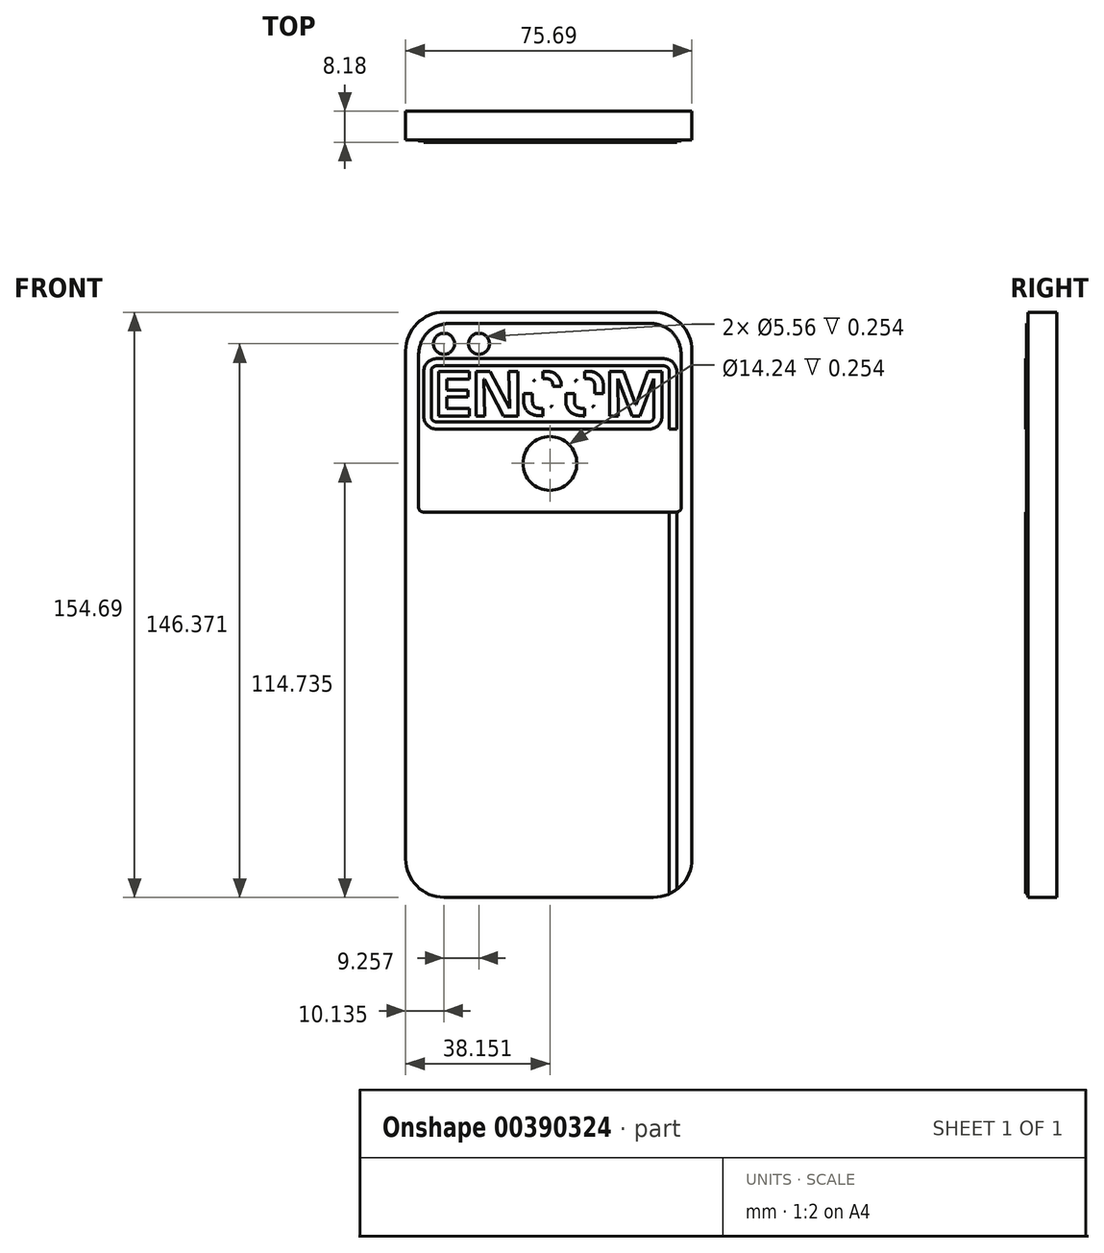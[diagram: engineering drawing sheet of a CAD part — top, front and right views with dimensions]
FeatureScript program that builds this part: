
annotation { "Feature Type Name" : "Feature", "Feature Type Description" : "" }
export const myFeature = defineFeature(function(context is Context, id is Id, definition is map)
    precondition{}
    {
        {
            var Q0;
            Q0=qCreatedBy(makeId("Front.planeOp"),FACE);
            var sketch = newSketch(context, id + "F0", { "sketchPlane" : qUnion([Q0])});
            skLineSegment(sketch, "E0.bottom", {"start": v(201.26, 129.6) * mm, "end": v(256.63, 129.6) * mm});
            skLineSegment(sketch, "E0.top", {"start": v(201.26, -25.09) * mm, "end": v(256.63, -25.09) * mm});
            skLineSegment(sketch, "E0.left", {"start": v(191.1, 119.44) * mm, "end": v(191.1, -14.93) * mm});
            skLineSegment(sketch, "E0.right", {"start": v(266.8, 119.44) * mm, "end": v(266.8, -14.93) * mm});
            skPoint(sketch, "E1.visualSharp", {"position": v(191.1, 129.6) * mm});
            skArc(sketch, "E1.filletArc", {"start": v(201.26, 129.6) * mm, "mid": v(194.08, 126.62) * mm, "end": v(191.1, 119.44) * mm});
            skPoint(sketch, "E2.visualSharp", {"position": v(266.8, 129.6) * mm});
            skArc(sketch, "E2.filletArc", {"start": v(266.8, 119.44) * mm, "mid": v(263.82, 126.62) * mm, "end": v(256.63, 129.6) * mm});
            skPoint(sketch, "E3.visualSharp", {"position": v(266.8, -25.09) * mm});
            skArc(sketch, "E3.filletArc", {"start": v(256.63, -25.09) * mm, "mid": v(263.82, -22.1) * mm, "end": v(266.8, -14.93) * mm});
            skPoint(sketch, "E4.visualSharp", {"position": v(191.1, -25.09) * mm});
            skArc(sketch, "E4.filletArc", {"start": v(191.1, -14.93) * mm, "mid": v(194.08, -22.1) * mm, "end": v(201.26, -25.09) * mm});
            skCircle(sketch, "E5", {"center": v(201.23, 121.28) * mm, "radius": 2.78 * mm});
            skCircle(sketch, "E6", {"center": v(210.5, 121.28) * mm, "radius": 2.78 * mm});
            skCircle(sketch, "E7", {"center": v(229.25, 89.64) * mm, "radius": 7.12 * mm});
            skLineSegment(sketch, "E8", {"start": v(229.25, 129.6) * mm, "end": v(229.25, -25.09) * mm});
            skLineSegment(sketch, "E9", {"start": v(229.25, 76.81) * mm, "end": v(195.67, 76.81) * mm});
            skLineSegment(sketch, "E10", {"start": v(194.55, 77.93) * mm, "end": v(194.55, 118.32) * mm});
            skPoint(sketch, "E11.visualSharp", {"position": v(194.55, 76.81) * mm});
            skArc(sketch, "E11.filletArc", {"start": v(194.55, 77.93) * mm, "mid": v(194.88, 77.14) * mm, "end": v(195.67, 76.81) * mm});
            skArc(sketch, "E12.MirrorCS", {"start": v(263.96, 77.93) * mm, "mid": v(263.63, 77.14) * mm, "end": v(262.83, 76.81) * mm});
            skLineSegment(sketch, "E13.MirrorCS", {"start": v(229.25, 76.81) * mm, "end": v(262.83, 76.81) * mm});
            skLineSegment(sketch, "E14.MirrorCS", {"start": v(263.96, 77.93) * mm, "end": v(263.96, 118.32) * mm});
            skLineSegment(sketch, "E15", {"start": v(195.67, 77.93) * mm, "end": v(229.25, 77.93) * mm});
            skLineSegment(sketch, "E16", {"start": v(195.67, 77.93) * mm, "end": v(195.67, 118.32) * mm});
            skLineSegment(sketch, "E17.MirrorCS", {"start": v(262.83, 77.93) * mm, "end": v(229.25, 77.93) * mm});
            skLineSegment(sketch, "E18.MirrorCS", {"start": v(262.83, 77.93) * mm, "end": v(262.83, 118.32) * mm});
            skLineSegment(sketch, "E19", {"start": v(229.25, 97.2) * mm, "end": v(195.67, 97.2) * mm});
            skLineSegment(sketch, "E20", {"start": v(195.67, 118.32) * mm, "end": v(229.25, 118.32) * mm});
            skArc(sketch, "E21", {"start": v(194.55, 118.32) * mm, "mid": v(194.96, 120.97) * mm, "end": v(196.15, 123.36) * mm});
            skArc(sketch, "E22", {"start": v(196.15, 123.36) * mm, "mid": v(197.4, 124.73) * mm, "end": v(198.94, 125.74) * mm});
            skArc(sketch, "E23", {"start": v(198.94, 125.74) * mm, "mid": v(200.66, 126.38) * mm, "end": v(202.48, 126.67) * mm});
            skLineSegment(sketch, "E24", {"start": v(202.48, 126.67) * mm, "end": v(229.25, 126.67) * mm});
            skLineSegment(sketch, "E25.MirrorCS", {"start": v(262.83, 118.32) * mm, "end": v(229.25, 118.32) * mm});
            skArc(sketch, "E26.MirrorCS", {"start": v(263.96, 118.32) * mm, "mid": v(263.55, 120.97) * mm, "end": v(262.36, 123.36) * mm});
            skArc(sketch, "E27.MirrorCS", {"start": v(262.36, 123.36) * mm, "mid": v(261.1, 124.73) * mm, "end": v(259.57, 125.74) * mm});
            skArc(sketch, "E28.MirrorCS", {"start": v(259.57, 125.74) * mm, "mid": v(257.84, 126.38) * mm, "end": v(256.02, 126.67) * mm});
            skLineSegment(sketch, "E29.MirrorCS", {"start": v(256.02, 126.67) * mm, "end": v(229.25, 126.67) * mm});
            skLineSegment(sketch, "E30.MirrorCS", {"start": v(229.25, 97.2) * mm, "end": v(262.83, 97.2) * mm});
            skSolve(sketch);
        }
        {
            var Q0;
            Q0=qSketchRegion(id+"F0",true);
            var Q1;
            Q1=makeQuery(id+"F0.imprint","IMPRINT",FACE,{"disambiguationData":[TD([[makeQuery(id+"F0.imprint","IMPRINT",EDGE,{"derivedFrom":sQuery(id+"F0.wireOp",EDGE,"E6")}),1.0]])]});
            var Q2;
            Q2=makeQuery(id+"F0.imprint","IMPRINT",FACE,{"disambiguationData":[TD([[makeQuery(id+"F0.imprint","IMPRINT",EDGE,{"derivedFrom":sQuery(id+"F0.wireOp",EDGE,"E5")}),1.0]])]});
            var Q3;
            {var subQ0=sQuery(id+"F0.wireOp",EDGE,"E19");Q3=makeQuery(id+"F0.imprint","IMPRINT",FACE,{"disambiguationData":[TD([[makeQuery(id+"F0.imprint","IMPRINT",EDGE,{"derivedFrom":subQ0}),-1.0]])]});}
            var Q4;
            {var subQ2=sQuery(id+"F0.wireOp",EDGE,"E25.MirrorCS");Q4=makeQuery(id+"F0.imprint","IMPRINT",FACE,{"disambiguationData":[TD([[makeQuery(id+"F0.imprint","IMPRINT",EDGE,{"derivedFrom":subQ2}),1.0]])]});}
            var Q5;
            {var subQ0=sQuery(id+"F0.wireOp",EDGE,"E17.MirrorCS");Q5=makeQuery(id+"F0.imprint","IMPRINT",FACE,{"disambiguationData":[TD([[makeQuery(id+"F0.imprint","IMPRINT",EDGE,{"derivedFrom":subQ0}),-1.0]])]});}
            var Q6;
            {var subQ0=sQuery(id+"F0.wireOp",EDGE,"E8");var subQ1=sQuery(id+"F0.wireOp",EDGE,"E7");var subQ2=makeQuery(id+"F0.imprint","INTERSECT",VERTEX,{"disambiguationData":[OD(0.0)],"derivedFrom":[subQ1,subQ0]});Q6=makeQuery(id+"F0.imprint","IMPRINT",FACE,{"disambiguationData":[TD([[makeQuery(id+"F0.imprint","IMPRINT",EDGE,{"disambiguationData":[TD([[subQ2,1.0]])],"derivedFrom":subQ1}),1.0]])]});}
            var Q7;
            {var subQ0=sQuery(id+"F0.wireOp",EDGE,"E8");var subQ1=sQuery(id+"F0.wireOp",EDGE,"E7");var subQ2=makeQuery(id+"F0.imprint","INTERSECT",VERTEX,{"disambiguationData":[OD(0.0)],"derivedFrom":[subQ1,subQ0]});Q7=makeQuery(id+"F0.imprint","IMPRINT",FACE,{"disambiguationData":[TD([[makeQuery(id+"F0.imprint","IMPRINT",EDGE,{"disambiguationData":[TD([[subQ2,-1.0]])],"derivedFrom":subQ1}),1.0]])]});}
            var Q8;
            {var subQ4=sQuery(id+"F0.wireOp",EDGE,"E13.MirrorCS");Q8=makeQuery(id+"F0.imprint","IMPRINT",FACE,{"disambiguationData":[TD([[makeQuery(id+"F0.imprint","IMPRINT",EDGE,{"derivedFrom":subQ4}),1.0]])]});}
            var Q9;
            Q9=makeQuery(id+"F0.imprint","IMPRINT",FACE,{"disambiguationData":[TD([[makeQuery(id+"F0.imprint","IMPRINT",EDGE,{"derivedFrom":sQuery(id+"F0.wireOp",EDGE,"E5")}),-1.0]])]});
            var Q10;
            {var subQ0=sQuery(id+"F0.wireOp",EDGE,"E15");Q10=makeQuery(id+"F0.imprint","IMPRINT",FACE,{"disambiguationData":[TD([[makeQuery(id+"F0.imprint","IMPRINT",EDGE,{"derivedFrom":subQ0}),1.0]])]});}
            extrude(context, id + "F1", {"entities" : qUnion([Q0, Q1, Q2, Q3, Q4, Q5, Q6, Q7, Q8, Q9, Q10]), "oppositeDirection" : true, "depth" : 7.62 * mm});
        }
        {
            var Q0;
            {var subQ4=sQuery(id+"F0.wireOp",EDGE,"E13.MirrorCS");Q0=makeQuery(id+"F0.imprint","IMPRINT",FACE,{"disambiguationData":[TD([[makeQuery(id+"F0.imprint","IMPRINT",EDGE,{"derivedFrom":subQ4}),1.0]])]});}
            var Q1;
            Q1=makeQuery(id+"F0.imprint","IMPRINT",FACE,{"disambiguationData":[TD([[makeQuery(id+"F0.imprint","IMPRINT",EDGE,{"derivedFrom":sQuery(id+"F0.wireOp",EDGE,"E5")}),-1.0]])]});
            var Q2;
            {var subQ0=sQuery(id+"F0.wireOp",EDGE,"E19");Q2=makeQuery(id+"F0.imprint","IMPRINT",FACE,{"disambiguationData":[TD([[makeQuery(id+"F0.imprint","IMPRINT",EDGE,{"derivedFrom":subQ0}),-1.0]])]});}
            var Q3;
            {var subQ0=sQuery(id+"F0.wireOp",EDGE,"E15");Q3=makeQuery(id+"F0.imprint","IMPRINT",FACE,{"disambiguationData":[TD([[makeQuery(id+"F0.imprint","IMPRINT",EDGE,{"derivedFrom":subQ0}),1.0]])]});}
            var Q4;
            {var subQ0=sQuery(id+"F0.wireOp",EDGE,"E17.MirrorCS");Q4=makeQuery(id+"F0.imprint","IMPRINT",FACE,{"disambiguationData":[TD([[makeQuery(id+"F0.imprint","IMPRINT",EDGE,{"derivedFrom":subQ0}),-1.0]])]});}
            var Q5;
            {var subQ2=sQuery(id+"F0.wireOp",EDGE,"E25.MirrorCS");Q5=makeQuery(id+"F0.imprint","IMPRINT",FACE,{"disambiguationData":[TD([[makeQuery(id+"F0.imprint","IMPRINT",EDGE,{"derivedFrom":subQ2}),1.0]])]});}
            var Q6;
            Q6=makeQuery(id+"F1.opExtrude","CAP_FACE",FACE,{"disambiguationData":[OSD([sQuery(id+"F0.wireOp",EDGE,"E0.bottom"),sQuery(id+"F0.wireOp",EDGE,"E0.top"),sQuery(id+"F0.wireOp",EDGE,"E0.left"),sQuery(id+"F0.wireOp",EDGE,"E0.right"),sQuery(id+"F0.wireOp",EDGE,"E1.filletArc"),sQuery(id+"F0.wireOp",EDGE,"E2.filletArc"),sQuery(id+"F0.wireOp",EDGE,"E3.filletArc"),sQuery(id+"F0.wireOp",EDGE,"E4.filletArc"),sQuery(id+"F0.wireOp",EDGE,"E9"),sQuery(id+"F0.wireOp",EDGE,"E10"),sQuery(id+"F0.wireOp",EDGE,"E11.filletArc"),sQuery(id+"F0.wireOp",EDGE,"E13.MirrorCS"),sQuery(id+"F0.wireOp",EDGE,"E12.MirrorCS"),sQuery(id+"F0.wireOp",EDGE,"E14.MirrorCS"),sQuery(id+"F0.wireOp",EDGE,"E21"),sQuery(id+"F0.wireOp",EDGE,"E22"),sQuery(id+"F0.wireOp",EDGE,"E23"),sQuery(id+"F0.wireOp",EDGE,"E24"),sQuery(id+"F0.wireOp",EDGE,"E26.MirrorCS"),sQuery(id+"F0.wireOp",EDGE,"E27.MirrorCS"),sQuery(id+"F0.wireOp",EDGE,"E28.MirrorCS"),sQuery(id+"F0.wireOp",EDGE,"E29.MirrorCS")])],"isStart":false});
            extrude(context, id + "F2", {"entities" : qUnion([Q0, Q1, Q2, Q3, Q4, Q5]), "endBoundEntityFace" : qUnion([Q6]), "depth" : 0.25 * mm});
        }
        {
            var Q0;
            Q0=qCreatedBy(makeId("Front.planeOp"),FACE);
            var sketch = newSketch(context, id + "F3", { "sketchPlane" : qUnion([Q0])});
            skLineSegment(sketch, "E31.bottom", {"start": v(195.87, 117.33) * mm, "end": v(197.87, 117.33) * mm});
            skLineSegment(sketch, "E31.top", {"start": v(195.87, 98.73) * mm, "end": v(197.87, 98.73) * mm});
            skLineSegment(sketch, "E31.left", {"start": v(195.87, 117.33) * mm, "end": v(195.87, 98.73) * mm});
            skLineSegment(sketch, "E32.bottom", {"start": v(195.87, 117.33) * mm, "end": v(262.8, 117.33) * mm});
            skLineSegment(sketch, "E32.left", {"start": v(195.87, 117.33) * mm, "end": v(195.87, 115.44) * mm});
            skLineSegment(sketch, "E32.right", {"start": v(262.8, 117.33) * mm, "end": v(262.8, 115.44) * mm});
            skLineSegment(sketch, "E33.bottom", {"start": v(195.87, 98.73) * mm, "end": v(262.8, 98.73) * mm});
            skLineSegment(sketch, "E33.left", {"start": v(195.87, 98.73) * mm, "end": v(195.87, 100.65) * mm});
            skLineSegment(sketch, "E33.right", {"start": v(262.8, 98.73) * mm, "end": v(262.8, 100.65) * mm});
            skLineSegment(sketch, "E34.bottom", {"start": v(262.8, 117.33) * mm, "end": v(260.8, 117.33) * mm});
            skLineSegment(sketch, "E34.top", {"start": v(262.8, 98.73) * mm, "end": v(260.8, 98.73) * mm});
            skLineSegment(sketch, "E34.left", {"start": v(262.8, 117.33) * mm, "end": v(262.8, 98.73) * mm});
            skLineSegment(sketch, "E35", {"start": v(260.8, 115.44) * mm, "end": v(261, 115.69) * mm});
            skLineSegment(sketch, "E36", {"start": v(197.87, 115.44) * mm, "end": v(197.6, 115.77) * mm});
            skLineSegment(sketch, "E37", {"start": v(197.87, 100.64) * mm, "end": v(197.7, 100.52) * mm});
            skLineSegment(sketch, "E38", {"start": v(195.87, 98.73) * mm, "end": v(195.56, 98.32) * mm});
            skLineSegment(sketch, "E39", {"start": v(195.87, 117.33) * mm, "end": v(195.2, 118.18) * mm});
            skLineSegment(sketch, "E40", {"start": v(262.8, 117.33) * mm, "end": v(263.3, 118) * mm});
            skLineSegment(sketch, "E41", {"start": v(262.8, 98.73) * mm, "end": v(263.5, 98.16) * mm});
            skLineSegment(sketch, "E42", {"start": v(258.9, 100.64) * mm, "end": v(259.43, 100.04) * mm});
            skLineSegment(sketch, "E43", {"start": v(260.8, 100.64) * mm, "end": v(261.23, 100.16) * mm});
            skLineSegment(sketch, "E44", {"start": v(197.87, 102.02) * mm, "end": v(197.87, 114.06) * mm});
            skLineSegment(sketch, "E45", {"start": v(199.25, 115.44) * mm, "end": v(259.41, 115.44) * mm});
            skLineSegment(sketch, "E46", {"start": v(260.8, 114.06) * mm, "end": v(260.8, 100.64) * mm});
            skPoint(sketch, "E47.visualSharp", {"position": v(260.8, 115.44) * mm});
            skArc(sketch, "E47.filletArc", {"start": v(260.8, 114.06) * mm, "mid": v(260.4, 115.04) * mm, "end": v(259.41, 115.44) * mm});
            skPoint(sketch, "E48.visualSharp", {"position": v(197.87, 115.44) * mm});
            skArc(sketch, "E48.filletArc", {"start": v(199.25, 115.44) * mm, "mid": v(198.27, 115.04) * mm, "end": v(197.87, 114.06) * mm});
            skLineSegment(sketch, "E49", {"start": v(256.76, 100.64) * mm, "end": v(257.05, 100.32) * mm});
            skLineSegment(sketch, "E50", {"start": v(255.38, 100.64) * mm, "end": v(199.25, 100.64) * mm});
            skPoint(sketch, "E51.visualSharp", {"position": v(197.87, 100.64) * mm});
            skArc(sketch, "E51.filletArc", {"start": v(197.87, 102.02) * mm, "mid": v(198.27, 101.04) * mm, "end": v(199.25, 100.64) * mm});
            skLineSegment(sketch, "E52", {"start": v(256.76, 102.02) * mm, "end": v(256.76, 112.1) * mm});
            skPoint(sketch, "E53.visualSharp", {"position": v(256.76, 100.64) * mm});
            skArc(sketch, "E53.filletArc", {"start": v(255.38, 100.64) * mm, "mid": v(256.36, 101.04) * mm, "end": v(256.76, 102.02) * mm});
            skLineSegment(sketch, "E54", {"start": v(262.8, 98.73) * mm, "end": v(262.8, 117.33) * mm});
            skLineSegment(sketch, "E55", {"start": v(262.8, 117.33) * mm, "end": v(195.87, 117.33) * mm});
            skLineSegment(sketch, "E56", {"start": v(199.76, 102.2) * mm, "end": v(256.76, 102.2) * mm});
            skLineSegment(sketch, "E57", {"start": v(199.76, 102.2) * mm, "end": v(199.76, 113.9) * mm});
            skLineSegment(sketch, "E58", {"start": v(199.76, 113.9) * mm, "end": v(220.72, 113.9) * mm});
            skLineSegment(sketch, "E59", {"start": v(220.72, 113.9) * mm, "end": v(220.72, 102.2) * mm});
            skLineSegment(sketch, "E60", {"start": v(211.79, 112) * mm, "end": v(212.02, 102.2) * mm});
            skLineSegment(sketch, "E61", {"start": v(211.79, 112) * mm, "end": v(211.87, 112) * mm});
            skLineSegment(sketch, "E62", {"start": v(211.87, 112) * mm, "end": v(216.92, 102.2) * mm});
            skLineSegment(sketch, "E63", {"start": v(218.62, 104.13) * mm, "end": v(218.43, 113.9) * mm});
            skLineSegment(sketch, "E64", {"start": v(218.62, 104.13) * mm, "end": v(218.56, 104.13) * mm});
            skLineSegment(sketch, "E65", {"start": v(218.56, 104.13) * mm, "end": v(213.46, 113.9) * mm});
            skLineSegment(sketch, "E66", {"start": v(209.7, 102.2) * mm, "end": v(209.7, 113.9) * mm});
            skLineSegment(sketch, "E67", {"start": v(207.92, 113.9) * mm, "end": v(207.92, 102.2) * mm});
            skLineSegment(sketch, "E68", {"start": v(202.04, 104.13) * mm, "end": v(207.92, 104.13) * mm});
            skLineSegment(sketch, "E69", {"start": v(202.04, 104.13) * mm, "end": v(202.04, 107.22) * mm});
            skLineSegment(sketch, "E70", {"start": v(202.04, 107.22) * mm, "end": v(207.92, 107.22) * mm});
            skLineSegment(sketch, "E71", {"start": v(202.04, 109.06) * mm, "end": v(207.92, 109.06) * mm});
            skLineSegment(sketch, "E72", {"start": v(202.04, 109.06) * mm, "end": v(202.04, 111.97) * mm});
            skLineSegment(sketch, "E73", {"start": v(202.04, 111.97) * mm, "end": v(207.92, 111.97) * mm});
            skLineSegment(sketch, "E74", {"start": v(207.6, 109.06) * mm, "end": v(207.6, 107.22) * mm});
            skLineSegment(sketch, "E75", {"start": v(245.04, 114) * mm, "end": v(245.04, 102.2) * mm});
            skLineSegment(sketch, "E76", {"start": v(245.04, 114) * mm, "end": v(248.72, 114) * mm});
            skLineSegment(sketch, "E77", {"start": v(248.72, 114) * mm, "end": v(251.93, 105.23) * mm});
            skLineSegment(sketch, "E78", {"start": v(251.93, 105.23) * mm, "end": v(252, 105.23) * mm});
            skLineSegment(sketch, "E79", {"start": v(252, 105.23) * mm, "end": v(255.18, 114) * mm});
            skLineSegment(sketch, "E80", {"start": v(255.18, 114) * mm, "end": v(258.9, 114) * mm});
            skLineSegment(sketch, "E81", {"start": v(258.9, 114) * mm, "end": v(258.9, 100.64) * mm});
            skLineSegment(sketch, "E82", {"start": v(247.33, 102.2) * mm, "end": v(247.15, 112) * mm});
            skLineSegment(sketch, "E83", {"start": v(247.15, 112) * mm, "end": v(247.2, 112) * mm});
            skLineSegment(sketch, "E84", {"start": v(247.2, 112) * mm, "end": v(250.97, 102.2) * mm});
            skLineSegment(sketch, "E85", {"start": v(253.01, 102.2) * mm, "end": v(256.76, 112.1) * mm});
            skLineSegment(sketch, "E86", {"start": v(220.72, 113.9) * mm, "end": v(245.04, 113.9) * mm});
            skLineSegment(sketch, "E87", {"start": v(227.34, 113.9) * mm, "end": v(227.34, 102.2) * mm});
            skLineSegment(sketch, "E88", {"start": v(238.42, 102.2) * mm, "end": v(238.42, 113.9) * mm});
            skLineSegment(sketch, "E89", {"start": v(238.42, 112.07) * mm, "end": v(239.01, 112.07) * mm});
            skArc(sketch, "E90", {"start": v(241.12, 110.12) * mm, "mid": v(240.45, 111.51) * mm, "end": v(239.01, 112.07) * mm});
            skArc(sketch, "E91", {"start": v(241.1, 110.32) * mm, "mid": v(240.5, 111.57) * mm, "end": v(239.22, 112.06) * mm});
            skArc(sketch, "E92", {"start": v(241.08, 110.47) * mm, "mid": v(240.62, 111.54) * mm, "end": v(239.57, 112.04) * mm});
            skArc(sketch, "E93", {"start": v(241.06, 110.68) * mm, "mid": v(240.74, 111.44) * mm, "end": v(240.07, 111.92) * mm});
            skArc(sketch, "E94", {"start": v(241, 110.94) * mm, "mid": v(240.64, 111.56) * mm, "end": v(240.02, 111.94) * mm});
            skArc(sketch, "E95", {"start": v(240.96, 111.06) * mm, "mid": v(240.67, 111.57) * mm, "end": v(240.17, 111.88) * mm});
            skArc(sketch, "E96", {"start": v(240.9, 111.23) * mm, "mid": v(240.72, 111.53) * mm, "end": v(240.45, 111.75) * mm});
            skPoint(sketch, "E96.endSnap0", {"position": v(240.45, 111.51) * mm});
            skLineSegment(sketch, "E97", {"start": v(207.6, 108.14) * mm, "end": v(245.04, 108.14) * mm});
            skLineSegment(sketch, "E98", {"start": v(241.12, 110.12) * mm, "end": v(241.12, 108.14) * mm});
            skArc(sketch, "E99.MirrorCS", {"start": v(240.9, 105.05) * mm, "mid": v(240.72, 104.75) * mm, "end": v(240.45, 104.54) * mm});
            skPoint(sketch, "E100.MirrorP", {"position": v(240.45, 104.78) * mm});
            skArc(sketch, "E101.MirrorCS", {"start": v(241.08, 105.81) * mm, "mid": v(240.62, 104.74) * mm, "end": v(239.57, 104.25) * mm});
            skArc(sketch, "E102.MirrorCS", {"start": v(241.1, 105.97) * mm, "mid": v(240.5, 104.72) * mm, "end": v(239.22, 104.22) * mm});
            skArc(sketch, "E103.MirrorCS", {"start": v(241.06, 105.6) * mm, "mid": v(240.74, 104.84) * mm, "end": v(240.07, 104.37) * mm});
            skArc(sketch, "E104.MirrorCS", {"start": v(241, 105.35) * mm, "mid": v(240.64, 104.72) * mm, "end": v(240.02, 104.35) * mm});
            skArc(sketch, "E105.MirrorCS", {"start": v(241.12, 106.17) * mm, "mid": v(240.45, 104.78) * mm, "end": v(239.01, 104.21) * mm});
            skArc(sketch, "E106.MirrorCS", {"start": v(240.96, 105.22) * mm, "mid": v(240.67, 104.72) * mm, "end": v(240.17, 104.4) * mm});
            skLineSegment(sketch, "E107.MirrorCS", {"start": v(241.12, 106.17) * mm, "end": v(241.12, 108.14) * mm});
            skLineSegment(sketch, "E108.MirrorCS", {"start": v(238.42, 104.21) * mm, "end": v(239.01, 104.21) * mm});
            skArc(sketch, "E109.MirrorCS", {"start": v(235.77, 105.6) * mm, "mid": v(236.1, 104.84) * mm, "end": v(236.76, 104.37) * mm});
            skArc(sketch, "E110.MirrorCS", {"start": v(235.87, 111.06) * mm, "mid": v(236.16, 111.57) * mm, "end": v(236.66, 111.88) * mm});
            skArc(sketch, "E111.MirrorCS", {"start": v(235.83, 110.94) * mm, "mid": v(236.2, 111.56) * mm, "end": v(236.81, 111.94) * mm});
            skArc(sketch, "E112.MirrorCS", {"start": v(235.83, 105.35) * mm, "mid": v(236.2, 104.72) * mm, "end": v(236.81, 104.35) * mm});
            skPoint(sketch, "E113.MirrorP", {"position": v(236.38, 104.78) * mm});
            skArc(sketch, "E114.MirrorCS", {"start": v(235.93, 111.23) * mm, "mid": v(236.11, 111.53) * mm, "end": v(236.38, 111.75) * mm});
            skArc(sketch, "E115.MirrorCS", {"start": v(235.7, 106.17) * mm, "mid": v(236.38, 104.78) * mm, "end": v(237.82, 104.21) * mm});
            skArc(sketch, "E116.MirrorCS", {"start": v(235.75, 110.47) * mm, "mid": v(236.2, 111.54) * mm, "end": v(237.26, 112.04) * mm});
            skArc(sketch, "E117.MirrorCS", {"start": v(235.75, 105.81) * mm, "mid": v(236.2, 104.74) * mm, "end": v(237.26, 104.25) * mm});
            skLineSegment(sketch, "E118.MirrorCS", {"start": v(235.7, 110.12) * mm, "end": v(235.7, 108.14) * mm});
            skPoint(sketch, "E119.MirrorP", {"position": v(236.38, 111.51) * mm});
            skArc(sketch, "E120.MirrorCS", {"start": v(235.77, 110.68) * mm, "mid": v(236.1, 111.44) * mm, "end": v(236.76, 111.92) * mm});
            skArc(sketch, "E121.MirrorCS", {"start": v(235.7, 110.12) * mm, "mid": v(236.38, 111.51) * mm, "end": v(237.82, 112.07) * mm});
            skLineSegment(sketch, "E122.MirrorCS", {"start": v(235.7, 106.17) * mm, "end": v(235.7, 108.14) * mm});
            skArc(sketch, "E123.MirrorCS", {"start": v(235.73, 105.97) * mm, "mid": v(236.32, 104.72) * mm, "end": v(237.61, 104.22) * mm});
            skArc(sketch, "E124.MirrorCS", {"start": v(235.73, 110.32) * mm, "mid": v(236.32, 111.57) * mm, "end": v(237.61, 112.06) * mm});
            skArc(sketch, "E125.MirrorCS", {"start": v(235.87, 105.22) * mm, "mid": v(236.16, 104.72) * mm, "end": v(236.66, 104.4) * mm});
            skArc(sketch, "E126.MirrorCS", {"start": v(235.93, 105.05) * mm, "mid": v(236.11, 104.75) * mm, "end": v(236.38, 104.54) * mm});
            skLineSegment(sketch, "E127.MirrorCS", {"start": v(238.42, 104.21) * mm, "end": v(237.82, 104.21) * mm});
            skLineSegment(sketch, "E128.MirrorCS", {"start": v(238.42, 112.07) * mm, "end": v(237.82, 112.07) * mm});
            skArc(sketch, "E129.MirrorCS", {"start": v(224.78, 111.06) * mm, "mid": v(225.08, 111.57) * mm, "end": v(225.57, 111.88) * mm});
            skArc(sketch, "E130.MirrorCS", {"start": v(224.74, 110.94) * mm, "mid": v(225.1, 111.56) * mm, "end": v(225.73, 111.94) * mm});
            skArc(sketch, "E131.MirrorCS", {"start": v(224.85, 111.23) * mm, "mid": v(225.03, 111.53) * mm, "end": v(225.3, 111.75) * mm});
            skArc(sketch, "E132.MirrorCS", {"start": v(224.66, 110.47) * mm, "mid": v(225.12, 111.54) * mm, "end": v(226.17, 112.04) * mm});
            skLineSegment(sketch, "E133.MirrorCS", {"start": v(224.62, 110.12) * mm, "end": v(224.62, 108.14) * mm});
            skArc(sketch, "E134.MirrorCS", {"start": v(224.69, 110.68) * mm, "mid": v(225, 111.44) * mm, "end": v(225.68, 111.92) * mm});
            skArc(sketch, "E135.MirrorCS", {"start": v(224.62, 110.12) * mm, "mid": v(225.3, 111.51) * mm, "end": v(226.73, 112.07) * mm});
            skArc(sketch, "E136.MirrorCS", {"start": v(224.65, 110.32) * mm, "mid": v(225.24, 111.57) * mm, "end": v(226.53, 112.06) * mm});
            skLineSegment(sketch, "E137.MirrorCS", {"start": v(227.33, 112.07) * mm, "end": v(226.73, 112.07) * mm});
            skArc(sketch, "E138.MirrorCS", {"start": v(224.78, 105.22) * mm, "mid": v(225.08, 104.72) * mm, "end": v(225.57, 104.4) * mm});
            skArc(sketch, "E139.MirrorCS", {"start": v(224.74, 105.35) * mm, "mid": v(225.1, 104.72) * mm, "end": v(225.73, 104.35) * mm});
            skArc(sketch, "E140.MirrorCS", {"start": v(224.69, 105.6) * mm, "mid": v(225, 104.84) * mm, "end": v(225.68, 104.37) * mm});
            skArc(sketch, "E141.MirrorCS", {"start": v(224.66, 105.81) * mm, "mid": v(225.12, 104.74) * mm, "end": v(226.17, 104.25) * mm});
            skArc(sketch, "E142.MirrorCS", {"start": v(224.62, 106.17) * mm, "mid": v(225.3, 104.78) * mm, "end": v(226.73, 104.21) * mm});
            skArc(sketch, "E143.MirrorCS", {"start": v(224.85, 105.05) * mm, "mid": v(225.03, 104.75) * mm, "end": v(225.3, 104.54) * mm});
            skArc(sketch, "E144.MirrorCS", {"start": v(224.65, 105.97) * mm, "mid": v(225.24, 104.72) * mm, "end": v(226.53, 104.22) * mm});
            skLineSegment(sketch, "E145.MirrorCS", {"start": v(227.33, 104.21) * mm, "end": v(226.73, 104.21) * mm});
            skLineSegment(sketch, "E146.MirrorCS", {"start": v(224.62, 106.17) * mm, "end": v(224.62, 108.14) * mm});
            skArc(sketch, "E147.MirrorCS", {"start": v(229.94, 105.35) * mm, "mid": v(229.57, 104.72) * mm, "end": v(228.95, 104.35) * mm});
            skArc(sketch, "E148.MirrorCS", {"start": v(229.9, 111.06) * mm, "mid": v(229.6, 111.57) * mm, "end": v(229.1, 111.88) * mm});
            skArc(sketch, "E149.MirrorCS", {"start": v(229.94, 110.94) * mm, "mid": v(229.57, 111.56) * mm, "end": v(228.95, 111.94) * mm});
            skArc(sketch, "E150.MirrorCS", {"start": v(229.9, 105.22) * mm, "mid": v(229.6, 104.72) * mm, "end": v(229.1, 104.4) * mm});
            skArc(sketch, "E151.MirrorCS", {"start": v(230.05, 110.12) * mm, "mid": v(229.38, 111.51) * mm, "end": v(227.94, 112.07) * mm});
            skArc(sketch, "E152.MirrorCS", {"start": v(230, 105.6) * mm, "mid": v(229.67, 104.84) * mm, "end": v(229, 104.37) * mm});
            skLineSegment(sketch, "E153.MirrorCS", {"start": v(230.05, 110.12) * mm, "end": v(230.05, 108.14) * mm});
            skArc(sketch, "E154.MirrorCS", {"start": v(230.03, 105.97) * mm, "mid": v(229.44, 104.72) * mm, "end": v(228.15, 104.22) * mm});
            skArc(sketch, "E155.MirrorCS", {"start": v(230, 110.68) * mm, "mid": v(229.67, 111.44) * mm, "end": v(229, 111.92) * mm});
            skArc(sketch, "E156.MirrorCS", {"start": v(230.01, 105.81) * mm, "mid": v(229.55, 104.74) * mm, "end": v(228.5, 104.25) * mm});
            skArc(sketch, "E157.MirrorCS", {"start": v(230.03, 110.32) * mm, "mid": v(229.44, 111.57) * mm, "end": v(228.15, 112.06) * mm});
            skArc(sketch, "E158.MirrorCS", {"start": v(230.01, 110.47) * mm, "mid": v(229.55, 111.54) * mm, "end": v(228.5, 112.04) * mm});
            skArc(sketch, "E159.MirrorCS", {"start": v(229.83, 111.23) * mm, "mid": v(229.65, 111.53) * mm, "end": v(229.38, 111.75) * mm});
            skArc(sketch, "E160.MirrorCS", {"start": v(229.83, 105.05) * mm, "mid": v(229.65, 104.75) * mm, "end": v(229.38, 104.54) * mm});
            skLineSegment(sketch, "E161.MirrorCS", {"start": v(230.05, 106.17) * mm, "end": v(230.05, 108.14) * mm});
            skArc(sketch, "E162.MirrorCS", {"start": v(230.05, 106.17) * mm, "mid": v(229.38, 104.78) * mm, "end": v(227.94, 104.21) * mm});
            skLineSegment(sketch, "E163.MirrorCS", {"start": v(227.35, 104.21) * mm, "end": v(227.94, 104.21) * mm});
            skLineSegment(sketch, "E164.MirrorCS", {"start": v(227.35, 112.07) * mm, "end": v(227.94, 112.07) * mm});
            skArc(sketch, "E165", {"start": v(243.36, 110.78) * mm, "mid": v(242.35, 112.87) * mm, "end": v(240.28, 113.9) * mm});
            skArc(sketch, "E166", {"start": v(243.34, 110.93) * mm, "mid": v(242.5, 112.87) * mm, "end": v(240.63, 113.84) * mm});
            skArc(sketch, "E167", {"start": v(243.1, 111.94) * mm, "mid": v(242.43, 113.05) * mm, "end": v(241.29, 113.68) * mm});
            skLineSegment(sketch, "E168", {"start": v(243.36, 110.78) * mm, "end": v(243.4, 110.21) * mm});
            skLineSegment(sketch, "E169", {"start": v(243.4, 110.21) * mm, "end": v(243.4, 108.14) * mm});
            skArc(sketch, "E170.MirrorCS", {"start": v(233.47, 110.78) * mm, "mid": v(234.48, 112.87) * mm, "end": v(236.55, 113.9) * mm});
            skArc(sketch, "E171.MirrorCS", {"start": v(233.73, 111.94) * mm, "mid": v(234.4, 113.05) * mm, "end": v(235.54, 113.68) * mm});
            skArc(sketch, "E172.MirrorCS", {"start": v(233.5, 110.93) * mm, "mid": v(234.32, 112.87) * mm, "end": v(236.2, 113.84) * mm});
            skLineSegment(sketch, "E173.MirrorCS", {"start": v(233.43, 110.21) * mm, "end": v(233.43, 108.14) * mm});
            skLineSegment(sketch, "E174.MirrorCS", {"start": v(233.47, 110.78) * mm, "end": v(233.43, 110.21) * mm});
            skLineSegment(sketch, "E175.MirrorCS", {"start": v(233.47, 105.5) * mm, "end": v(233.43, 106.07) * mm});
            skLineSegment(sketch, "E176.MirrorCS", {"start": v(233.43, 106.07) * mm, "end": v(233.43, 108.14) * mm});
            skArc(sketch, "E177.MirrorCS", {"start": v(233.47, 105.5) * mm, "mid": v(234.48, 103.42) * mm, "end": v(236.55, 102.38) * mm});
            skArc(sketch, "E178.MirrorCS", {"start": v(233.73, 104.35) * mm, "mid": v(234.4, 103.23) * mm, "end": v(235.54, 102.6) * mm});
            skArc(sketch, "E179.MirrorCS", {"start": v(233.5, 105.36) * mm, "mid": v(234.32, 103.42) * mm, "end": v(236.2, 102.44) * mm});
            skLineSegment(sketch, "E180.MirrorCS", {"start": v(243.36, 105.5) * mm, "end": v(243.4, 106.07) * mm});
            skArc(sketch, "E181.MirrorCS", {"start": v(243.36, 105.5) * mm, "mid": v(242.35, 103.42) * mm, "end": v(240.28, 102.38) * mm});
            skArc(sketch, "E182.MirrorCS", {"start": v(243.34, 105.36) * mm, "mid": v(242.5, 103.42) * mm, "end": v(240.63, 102.44) * mm});
            skArc(sketch, "E183.MirrorCS", {"start": v(243.1, 104.35) * mm, "mid": v(242.43, 103.23) * mm, "end": v(241.29, 102.6) * mm});
            skLineSegment(sketch, "E184.MirrorCS", {"start": v(243.4, 106.07) * mm, "end": v(243.4, 108.14) * mm});
            skArc(sketch, "E185", {"start": v(236.55, 102.38) * mm, "mid": v(238.42, 102.2) * mm, "end": v(240.28, 102.38) * mm});
            skLineSegment(sketch, "E186", {"start": v(227.33, 112.07) * mm, "end": v(227.35, 112.07) * mm});
            skLineSegment(sketch, "E187", {"start": v(227.33, 104.21) * mm, "end": v(227.35, 104.21) * mm});
            skArc(sketch, "E188", {"start": v(232.2, 110.78) * mm, "mid": v(231.2, 112.87) * mm, "end": v(229.13, 113.9) * mm});
            skArc(sketch, "E189", {"start": v(232.19, 110.93) * mm, "mid": v(231.36, 112.87) * mm, "end": v(229.48, 113.84) * mm});
            skArc(sketch, "E190", {"start": v(231.95, 111.94) * mm, "mid": v(231.28, 113.05) * mm, "end": v(230.14, 113.68) * mm});
            skLineSegment(sketch, "E191", {"start": v(232.2, 110.78) * mm, "end": v(232.25, 110.21) * mm});
            skLineSegment(sketch, "E192", {"start": v(232.25, 110.21) * mm, "end": v(232.25, 108.14) * mm});
            skArc(sketch, "E193.MirrorCS", {"start": v(222.32, 110.78) * mm, "mid": v(223.33, 112.87) * mm, "end": v(225.4, 113.9) * mm});
            skArc(sketch, "E194.MirrorCS", {"start": v(222.58, 111.94) * mm, "mid": v(223.25, 113.05) * mm, "end": v(224.4, 113.68) * mm});
            skArc(sketch, "E195.MirrorCS", {"start": v(222.34, 110.93) * mm, "mid": v(223.17, 112.87) * mm, "end": v(225.05, 113.84) * mm});
            skLineSegment(sketch, "E196.MirrorCS", {"start": v(222.28, 110.21) * mm, "end": v(222.28, 108.14) * mm});
            skLineSegment(sketch, "E197.MirrorCS", {"start": v(222.32, 110.78) * mm, "end": v(222.28, 110.21) * mm});
            skLineSegment(sketch, "E198.MirrorCS", {"start": v(222.32, 105.51) * mm, "end": v(222.28, 106.07) * mm});
            skLineSegment(sketch, "E199.MirrorCS", {"start": v(222.28, 106.07) * mm, "end": v(222.28, 108.14) * mm});
            skArc(sketch, "E200.MirrorCS", {"start": v(222.32, 105.51) * mm, "mid": v(223.33, 103.42) * mm, "end": v(225.4, 102.38) * mm});
            skArc(sketch, "E201.MirrorCS", {"start": v(222.58, 104.35) * mm, "mid": v(223.25, 103.23) * mm, "end": v(224.4, 102.6) * mm});
            skArc(sketch, "E202.MirrorCS", {"start": v(222.34, 105.36) * mm, "mid": v(223.17, 103.42) * mm, "end": v(225.05, 102.45) * mm});
            skLineSegment(sketch, "E203.MirrorCS", {"start": v(232.2, 105.51) * mm, "end": v(232.25, 106.07) * mm});
            skArc(sketch, "E204.MirrorCS", {"start": v(232.2, 105.51) * mm, "mid": v(231.2, 103.42) * mm, "end": v(229.13, 102.38) * mm});
            skArc(sketch, "E205.MirrorCS", {"start": v(232.19, 105.36) * mm, "mid": v(231.36, 103.42) * mm, "end": v(229.48, 102.45) * mm});
            skArc(sketch, "E206.MirrorCS", {"start": v(231.95, 104.35) * mm, "mid": v(231.28, 103.23) * mm, "end": v(230.14, 102.6) * mm});
            skLineSegment(sketch, "E207.MirrorCS", {"start": v(232.25, 106.07) * mm, "end": v(232.25, 108.14) * mm});
            skArc(sketch, "E208", {"start": v(225.4, 102.38) * mm, "mid": v(227.26, 102.2) * mm, "end": v(229.13, 102.38) * mm});
            skLineSegment(sketch, "E209", {"start": v(230.05, 110) * mm, "end": v(232.25, 110) * mm});
            skLineSegment(sketch, "E210.MirrorCS", {"start": v(230.05, 106.3) * mm, "end": v(232.25, 106.3) * mm});
            skLineSegment(sketch, "E211", {"start": v(260.8, 100.64) * mm, "end": v(260.8, 98.73) * mm});
            skLineSegment(sketch, "E212", {"start": v(255.38, 100.64) * mm, "end": v(255.38, 98.73) * mm});
            skLineSegment(sketch, "E213", {"start": v(256.76, 102.02) * mm, "end": v(258.9, 102.02) * mm});
            skArc(sketch, "E214", {"start": v(255.38, 98.73) * mm, "mid": v(257.83, 99.64) * mm, "end": v(258.9, 102.02) * mm});
            skLineSegment(sketch, "E215", {"start": v(199.25, 100.64) * mm, "end": v(199.25, 98.73) * mm});
            skLineSegment(sketch, "E216", {"start": v(197.87, 102.02) * mm, "end": v(195.87, 102.02) * mm});
            skLineSegment(sketch, "E217", {"start": v(197.87, 114.06) * mm, "end": v(195.87, 114.06) * mm});
            skLineSegment(sketch, "E218", {"start": v(199.25, 115.44) * mm, "end": v(199.25, 117.33) * mm});
            skLineSegment(sketch, "E219", {"start": v(259.41, 115.44) * mm, "end": v(259.41, 117.33) * mm});
            skLineSegment(sketch, "E220", {"start": v(260.8, 114.06) * mm, "end": v(262.8, 114.06) * mm});
            skArc(sketch, "E221", {"start": v(195.87, 102.02) * mm, "mid": v(196.9, 99.7) * mm, "end": v(199.25, 98.73) * mm});
            skArc(sketch, "E222", {"start": v(199.25, 117.33) * mm, "mid": v(196.9, 116.39) * mm, "end": v(195.87, 114.06) * mm});
            skArc(sketch, "E223", {"start": v(262.8, 114.06) * mm, "mid": v(261.77, 116.38) * mm, "end": v(259.41, 117.33) * mm});
            skLineSegment(sketch, "E224.bottom", {"start": v(260.8, 98.73) * mm, "end": v(262.8, 98.73) * mm});
            skLineSegment(sketch, "E224.top", {"start": v(260.8, 76.81) * mm, "end": v(262.8, 76.81) * mm});
            skLineSegment(sketch, "E224.left", {"start": v(260.8, 98.73) * mm, "end": v(260.8, 76.81) * mm});
            skLineSegment(sketch, "E224.right", {"start": v(262.8, 98.73) * mm, "end": v(262.8, 76.81) * mm});
            skLineSegment(sketch, "E225", {"start": v(260.8, 76.81) * mm, "end": v(260.8, -24.12) * mm});
            skLineSegment(sketch, "E226", {"start": v(262.8, 76.81) * mm, "end": v(262.8, -22.93) * mm});
            skPoint(sketch, "E226.endSnap0", {"position": v(262.8, 108.03) * mm});
            skArc(sketch, "E227", {"start": v(260.8, -24.12) * mm, "mid": v(261.83, -23.58) * mm, "end": v(262.8, -22.93) * mm});
            skSolve(sketch);
        }
        {
            var Q0;
            {var subQ7=sQuery(id+"F3.wireOp",EDGE,"E57");Q0=makeQuery(id+"F3.imprint","IMPRINT",FACE,{"disambiguationData":[TD([[makeQuery(id+"F3.imprint","IMPRINT",EDGE,{"derivedFrom":subQ7}),-1.0]])]});}
            var Q1;
            {var subQ2=sQuery(id+"F3.wireOp",EDGE,"E59");Q1=makeQuery(id+"F3.imprint","IMPRINT",FACE,{"disambiguationData":[TD([[makeQuery(id+"F3.imprint","IMPRINT",EDGE,{"derivedFrom":subQ2}),-1.0]])]});}
            var Q2;
            {var subQ0=sQuery(id+"F3.wireOp",EDGE,"E64");Q2=makeQuery(id+"F3.imprint","IMPRINT",FACE,{"disambiguationData":[TD([[makeQuery(id+"F3.imprint","IMPRINT",EDGE,{"derivedFrom":subQ0}),1.0]])]});}
            var Q3;
            {var subQ1=sQuery(id+"F3.wireOp",EDGE,"E61");Q3=makeQuery(id+"F3.imprint","IMPRINT",FACE,{"disambiguationData":[TD([[makeQuery(id+"F3.imprint","IMPRINT",EDGE,{"derivedFrom":subQ1}),1.0]])]});}
            var Q4;
            {var subQ0=sQuery(id+"F3.wireOp",EDGE,"E60");var subQ1=sQuery(id+"F3.wireOp",EDGE,"E56");var subQ2=makeQuery(id+"F3.imprint","INTERSECT",VERTEX,{"derivedFrom":[subQ1,subQ0]});Q4=makeQuery(id+"F3.imprint","IMPRINT",FACE,{"disambiguationData":[TD([[makeQuery(id+"F3.imprint","IMPRINT",EDGE,{"disambiguationData":[TD([[subQ2,1.0]])],"derivedFrom":subQ1}),1.0]])]});}
            var Q5;
            {var subQ0=sQuery(id+"F3.wireOp",EDGE,"E114.MirrorCS");Q5=makeQuery(id+"F3.imprint","IMPRINT",FACE,{"disambiguationData":[TD([[makeQuery(id+"F3.imprint","IMPRINT",EDGE,{"derivedFrom":subQ0}),1.0]])]});}
            var Q6;
            {var subQ13=sQuery(id+"F3.wireOp",EDGE,"E89");Q6=makeQuery(id+"F3.imprint","IMPRINT",FACE,{"disambiguationData":[TD([[makeQuery(id+"F3.imprint","IMPRINT",EDGE,{"derivedFrom":subQ13}),1.0]])]});}
            var Q7;
            {var subQ24=sQuery(id+"F3.wireOp",EDGE,"E99.MirrorCS");Q7=makeQuery(id+"F3.imprint","IMPRINT",FACE,{"disambiguationData":[TD([[makeQuery(id+"F3.imprint","IMPRINT",EDGE,{"derivedFrom":subQ24}),1.0]])]});}
            var Q8;
            {var subQ0=sQuery(id+"F3.wireOp",EDGE,"E122.MirrorCS");Q8=makeQuery(id+"F3.imprint","IMPRINT",FACE,{"disambiguationData":[TD([[makeQuery(id+"F3.imprint","IMPRINT",EDGE,{"derivedFrom":subQ0}),1.0]])]});}
            var Q9;
            {var subQ23=sQuery(id+"F3.wireOp",EDGE,"E159.MirrorCS");Q9=makeQuery(id+"F3.imprint","IMPRINT",FACE,{"disambiguationData":[TD([[makeQuery(id+"F3.imprint","IMPRINT",EDGE,{"derivedFrom":subQ23}),-1.0]])]});}
            var Q10;
            {var subQ28=sQuery(id+"F3.wireOp",EDGE,"E131.MirrorCS");Q10=makeQuery(id+"F3.imprint","IMPRINT",FACE,{"disambiguationData":[TD([[makeQuery(id+"F3.imprint","IMPRINT",EDGE,{"derivedFrom":subQ28}),1.0]])]});}
            var Q11;
            {var subQ19=sQuery(id+"F3.wireOp",EDGE,"E143.MirrorCS");Q11=makeQuery(id+"F3.imprint","IMPRINT",FACE,{"disambiguationData":[TD([[makeQuery(id+"F3.imprint","IMPRINT",EDGE,{"derivedFrom":subQ19}),-1.0]])]});}
            var Q12;
            {var subQ23=sQuery(id+"F3.wireOp",EDGE,"E160.MirrorCS");Q12=makeQuery(id+"F3.imprint","IMPRINT",FACE,{"disambiguationData":[TD([[makeQuery(id+"F3.imprint","IMPRINT",EDGE,{"derivedFrom":subQ23}),1.0]])]});}
            var Q13;
            {var subQ5=sQuery(id+"F3.wireOp",EDGE,"E76");Q13=makeQuery(id+"F3.imprint","IMPRINT",FACE,{"disambiguationData":[TD([[makeQuery(id+"F3.imprint","IMPRINT",EDGE,{"derivedFrom":subQ5}),-1.0]])]});}
            var Q14;
            Q14=makeQuery(id+"F3.imprint","IMPRINT",FACE,{"disambiguationData":[TD([[makeQuery(id+"F3.imprint","IMPRINT",EDGE,{"derivedFrom":sQuery(id+"F3.wireOp",EDGE,"E53.filletArc")}),-1.0]])]});
            var Q15;
            Q15=makeQuery(id+"F3.imprint","IMPRINT",FACE,{"disambiguationData":[TD([[makeQuery(id+"F3.imprint","IMPRINT",EDGE,{"derivedFrom":sQuery(id+"F3.wireOp",EDGE,"E50")}),1.0]])]});
            var Q16;
            Q16=makeQuery(id+"F3.imprint","IMPRINT",FACE,{"disambiguationData":[TD([[makeQuery(id+"F3.imprint","IMPRINT",EDGE,{"derivedFrom":sQuery(id+"F3.wireOp",EDGE,"E44")}),1.0]])]});
            var Q17;
            Q17=makeQuery(id+"F3.imprint","IMPRINT",FACE,{"disambiguationData":[TD([[makeQuery(id+"F3.imprint","IMPRINT",EDGE,{"derivedFrom":sQuery(id+"F3.wireOp",EDGE,"E51.filletArc")}),-1.0]])]});
            var Q18;
            Q18=makeQuery(id+"F3.imprint","IMPRINT",FACE,{"disambiguationData":[TD([[makeQuery(id+"F3.imprint","IMPRINT",EDGE,{"derivedFrom":sQuery(id+"F3.wireOp",EDGE,"E48.filletArc")}),-1.0]])]});
            var Q19;
            Q19=makeQuery(id+"F3.imprint","IMPRINT",FACE,{"disambiguationData":[TD([[makeQuery(id+"F3.imprint","IMPRINT",EDGE,{"derivedFrom":sQuery(id+"F3.wireOp",EDGE,"E45")}),1.0]])]});
            var Q20;
            Q20=makeQuery(id+"F3.imprint","IMPRINT",FACE,{"disambiguationData":[TD([[makeQuery(id+"F3.imprint","IMPRINT",EDGE,{"derivedFrom":sQuery(id+"F3.wireOp",EDGE,"E47.filletArc")}),-1.0]])]});
            var Q21;
            Q21=makeQuery(id+"F3.imprint","IMPRINT",FACE,{"disambiguationData":[TD([[makeQuery(id+"F3.imprint","IMPRINT",EDGE,{"derivedFrom":sQuery(id+"F3.wireOp",EDGE,"E46")}),1.0]])]});
            var Q22;
            Q22=makeQuery(id+"F3.imprint","IMPRINT",FACE,{"disambiguationData":[TD([[makeQuery(id+"F3.imprint","IMPRINT",EDGE,{"derivedFrom":sQuery(id+"F3.wireOp",EDGE,"E224.bottom")}),-1.0]])]});
            var Q23;
            Q23=makeQuery(id+"F3.imprint","IMPRINT",FACE,{"disambiguationData":[TD([[makeQuery(id+"F3.imprint","IMPRINT",EDGE,{"derivedFrom":sQuery(id+"F3.wireOp",EDGE,"E224.top")}),-1.0]])]});
            extrude(context, id + "F4", {"entities" : qUnion([Q0, Q1, Q2, Q3, Q4, Q5, Q6, Q7, Q8, Q9, Q10, Q11, Q12, Q13, Q14, Q15, Q16, Q17, Q18, Q19, Q20, Q21, Q22, Q23]), "operationType" : NewBodyOperationType.ADD, "depth" : 0.56 * mm});
        }
    });
